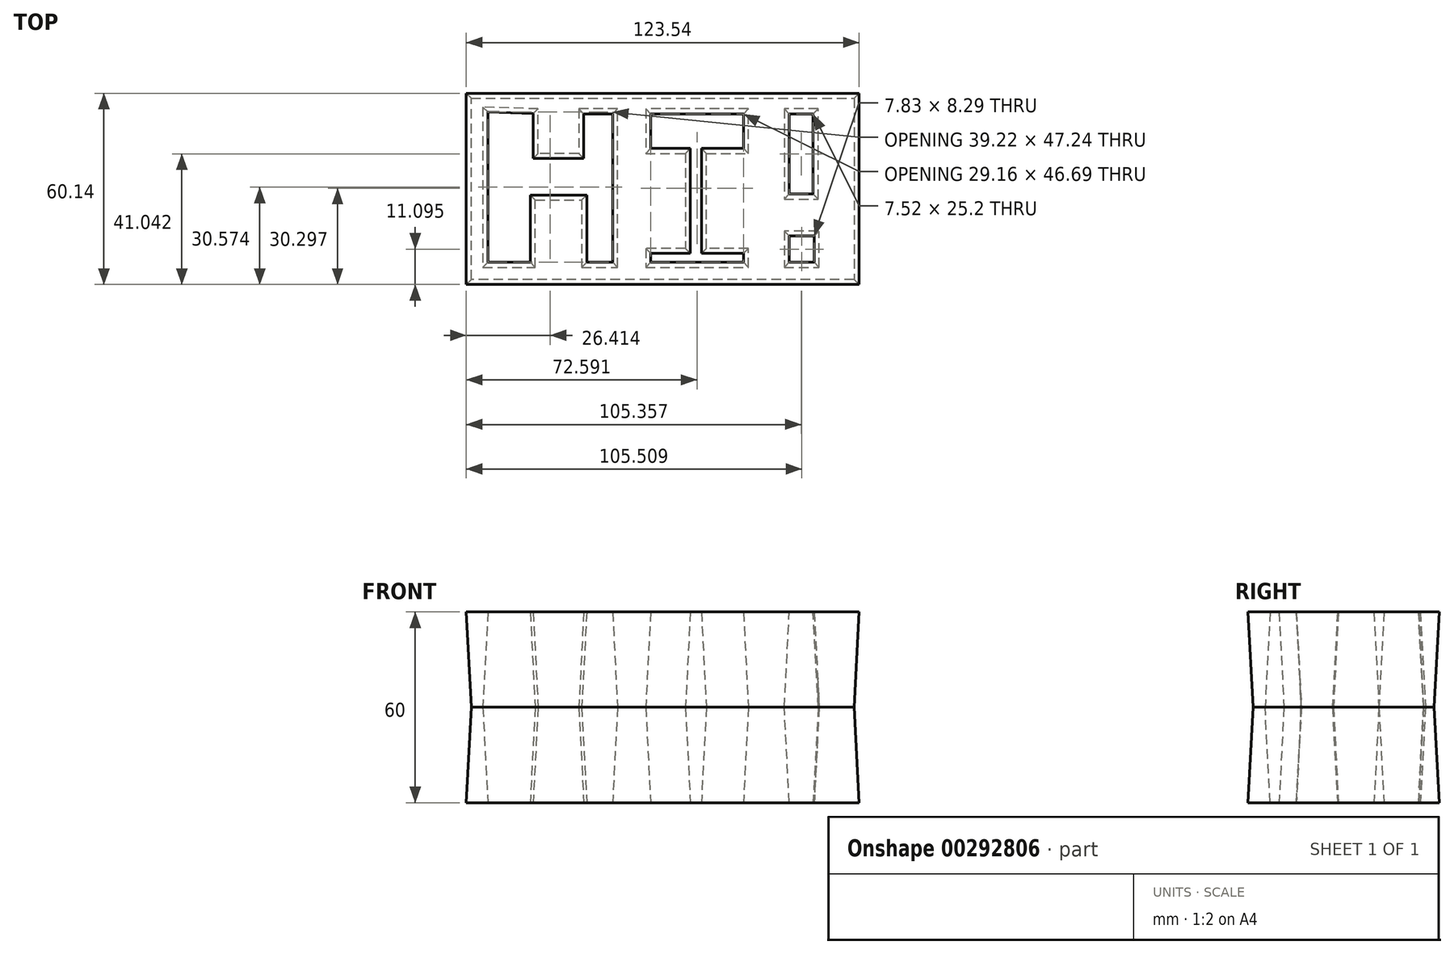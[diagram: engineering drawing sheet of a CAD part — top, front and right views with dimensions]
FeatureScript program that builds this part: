
annotation { "Feature Type Name" : "Feature", "Feature Type Description" : "" }
export const myFeature = defineFeature(function(context is Context, id is Id, definition is map)
    precondition{}
    {
        {
            var Q0;
            Q0=qCreatedBy(makeId("Top.planeOp"),FACE);
            var sketch = newSketch(context, id + "F0", { "sketchPlane" : qUnion([Q0])});
            skLineSegment(sketch, "E0", {"start": v(-70.29, 50.44) * mm, "end": v(-70.29, 0) * mm});
            skLineSegment(sketch, "E1", {"start": v(-70.29, 0) * mm, "end": v(-53.83, 0) * mm});
            skLineSegment(sketch, "E2", {"start": v(-53.83, 0) * mm, "end": v(-53.83, 21.18) * mm});
            skLineSegment(sketch, "E3", {"start": v(-53.83, 21.18) * mm, "end": v(-39.2, 21.18) * mm});
            skLineSegment(sketch, "E4", {"start": v(-39.2, 21.18) * mm, "end": v(-39.2, 0) * mm});
            skLineSegment(sketch, "E5", {"start": v(-39.2, 0) * mm, "end": v(-27.92, 0) * mm});
            skLineSegment(sketch, "E6", {"start": v(-27.92, 0) * mm, "end": v(-27.92, 49.83) * mm});
            skLineSegment(sketch, "E7", {"start": v(-27.92, 49.83) * mm, "end": v(-40.11, 49.83) * mm});
            skLineSegment(sketch, "E8", {"start": v(-40.11, 49.83) * mm, "end": v(-40.11, 35.81) * mm});
            skLineSegment(sketch, "E9", {"start": v(-40.11, 35.81) * mm, "end": v(-52.92, 35.81) * mm});
            skLineSegment(sketch, "E10", {"start": v(-52.92, 35.81) * mm, "end": v(-52.92, 49.83) * mm});
            skLineSegment(sketch, "E11", {"start": v(-52.92, 49.83) * mm, "end": v(-70.29, 50.44) * mm});
            skPoint(sketch, "E12.end.orphan", {"position": v(-21.52, 35.81) * mm});
            skPoint(sketch, "E12.start.orphan", {"position": v(-19.08, 49.83) * mm});
            skLineSegment(sketch, "E13", {"start": v(-19.08, 49.83) * mm, "end": v(-19.08, 35.81) * mm});
            skLineSegment(sketch, "E14", {"start": v(-19.08, 35.81) * mm, "end": v(-6.59, 35.81) * mm});
            skLineSegment(sketch, "E15", {"start": v(-6.59, 35.81) * mm, "end": v(-6.59, 5.94) * mm});
            skLineSegment(sketch, "E16", {"start": v(-6.59, 5.94) * mm, "end": v(-19.08, 5.94) * mm});
            skLineSegment(sketch, "E17", {"start": v(-19.08, 5.94) * mm, "end": v(-19.08, 0) * mm});
            skLineSegment(sketch, "E18", {"start": v(-19.08, 0) * mm, "end": v(13.23, 0) * mm});
            skLineSegment(sketch, "E19", {"start": v(13.23, 0) * mm, "end": v(13.23, 5.94) * mm});
            skLineSegment(sketch, "E20", {"start": v(13.23, 5.94) * mm, "end": v(0, 5.94) * mm});
            skLineSegment(sketch, "E21", {"start": v(0, 5.94) * mm, "end": v(0, 35.81) * mm});
            skLineSegment(sketch, "E22", {"start": v(0, 35.81) * mm, "end": v(13.23, 35.81) * mm});
            skLineSegment(sketch, "E23", {"start": v(13.23, 35.81) * mm, "end": v(13.23, 49.83) * mm});
            skLineSegment(sketch, "E24", {"start": v(13.23, 49.83) * mm, "end": v(-19.08, 49.83) * mm});
            skLineSegment(sketch, "E25", {"start": v(24.5, 49.83) * mm, "end": v(24.5, 21.49) * mm});
            skLineSegment(sketch, "E26", {"start": v(24.5, 21.49) * mm, "end": v(35.17, 21.49) * mm});
            skLineSegment(sketch, "E27", {"start": v(35.17, 21.49) * mm, "end": v(35.17, 49.83) * mm});
            skLineSegment(sketch, "E28", {"start": v(24.5, 49.83) * mm, "end": v(35.17, 49.83) * mm});
            skLineSegment(sketch, "E29", {"start": v(24.5, 11.43) * mm, "end": v(24.5, 0) * mm});
            skLineSegment(sketch, "E30", {"start": v(24.5, 11.43) * mm, "end": v(35.17, 11.43) * mm});
            skLineSegment(sketch, "E31", {"start": v(35.48, 11.13) * mm, "end": v(35.48, 0) * mm});
            skLineSegment(sketch, "E32", {"start": v(35.48, 0) * mm, "end": v(24.5, 0) * mm});
            skLineSegment(sketch, "E33.bottom", {"start": v(-73.95, 53.19) * mm, "end": v(46.45, 53.19) * mm});
            skLineSegment(sketch, "E33.top", {"start": v(-73.95, -3.81) * mm, "end": v(46.45, -3.81) * mm});
            skLineSegment(sketch, "E33.left", {"start": v(-73.95, 53.19) * mm, "end": v(-73.95, -3.81) * mm});
            skLineSegment(sketch, "E33.right", {"start": v(46.45, 53.19) * mm, "end": v(46.45, -3.81) * mm});
            skLineSegment(sketch, "E34", {"start": v(35.17, 11.43) * mm, "end": v(35.48, 11.13) * mm});
            skSolve(sketch);
        }
        {
            var Q0;
            Q0 = qSketchRegion(id + "F0", true);
            extrude(context, id + "F1", {"entities" : qUnion([Q0]), "depth" : 30 * mm, "hasDraft" : true, "draftAngle" : 3 * degree, "hasSecondDirection" : true, "secondDirectionOppositeDirection" : true, "secondDirectionDepth" : 30 * mm, "hasSecondDirectionDraft" : true, "secondDirectionDraftAngle" : 3 * degree});
        }
    });
